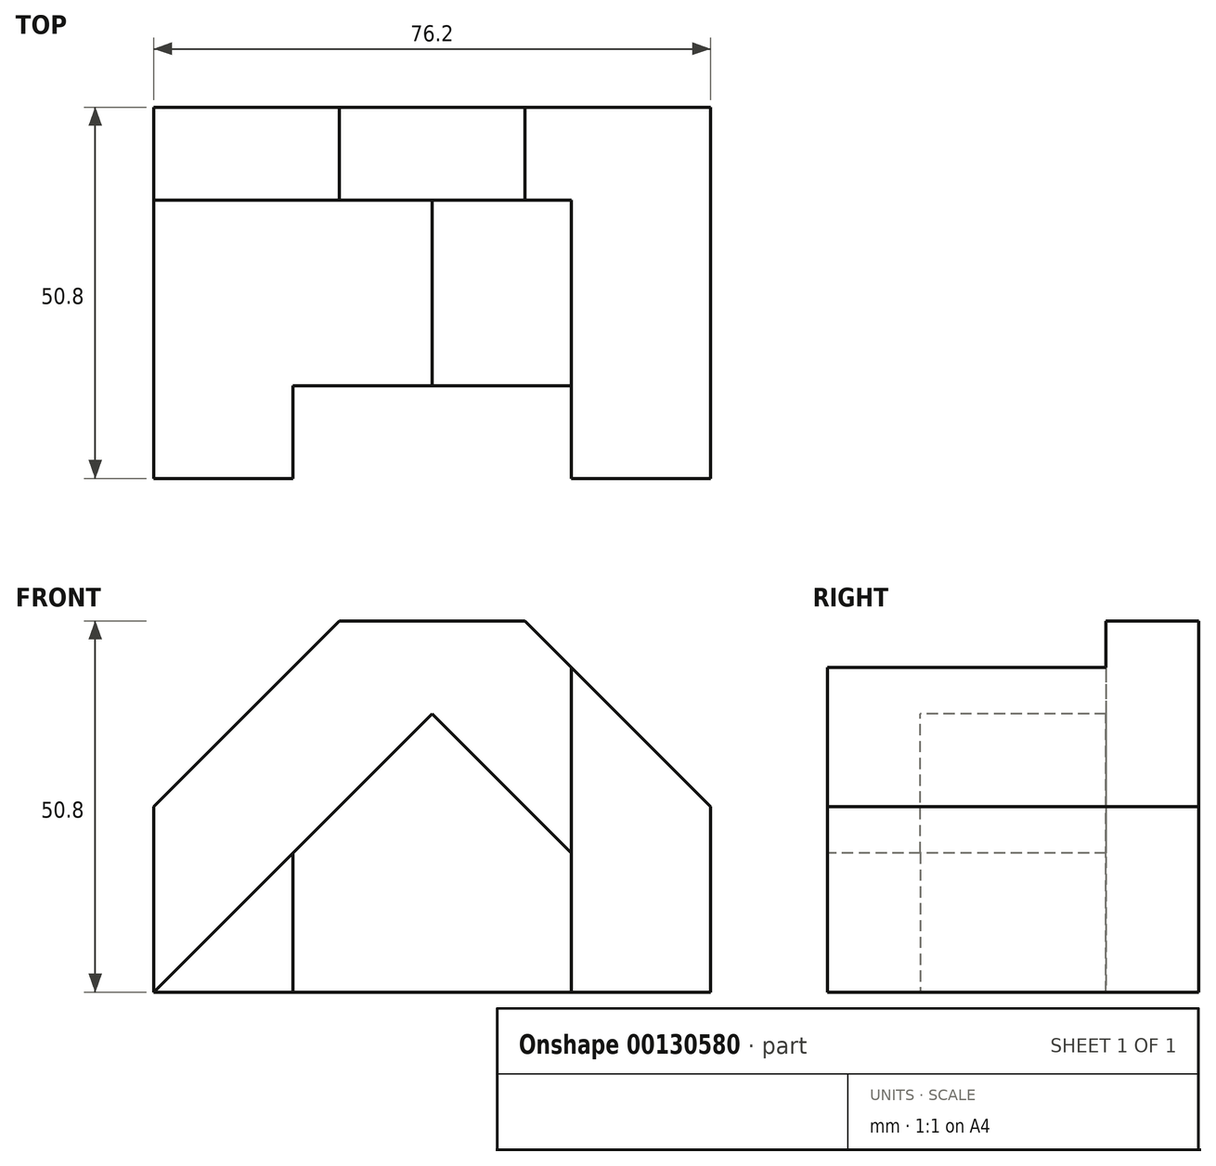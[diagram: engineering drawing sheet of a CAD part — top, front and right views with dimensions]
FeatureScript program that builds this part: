
annotation { "Feature Type Name" : "Feature", "Feature Type Description" : "" }
export const myFeature = defineFeature(function(context is Context, id is Id, definition is map)
    precondition{}
    {
        {
            var Q0;
            Q0=qCreatedBy(makeId("Top.planeOp"),FACE);
            var sketch = newSketch(context, id + "F0", { "sketchPlane" : qUnion([Q0])});
            skLineSegment(sketch, "E0", {"start": v(0, 0) * mm, "end": v(-38.1, 0) * mm});
            skLineSegment(sketch, "E1", {"start": v(-38.1, 0) * mm, "end": v(-38.1, 12.7) * mm});
            skLineSegment(sketch, "E2", {"start": v(-38.1, 12.7) * mm, "end": v(38.1, 12.7) * mm});
            skLineSegment(sketch, "E3", {"start": v(38.1, 12.7) * mm, "end": v(38.1, 0) * mm});
            skLineSegment(sketch, "E4", {"start": v(38.1, 0) * mm, "end": v(0, 0) * mm});
            skLineSegment(sketch, "E5", {"start": v(-19.05, 0) * mm, "end": v(-19.05, 12.7) * mm});
            skLineSegment(sketch, "E6", {"start": v(6.35, 12.7) * mm, "end": v(6.35, 0) * mm});
            skLineSegment(sketch, "E7", {"start": v(-38.1, 0) * mm, "end": v(-38.1, -38.1) * mm});
            skLineSegment(sketch, "E8", {"start": v(38.1, -38.1) * mm, "end": v(38.1, 0) * mm});
            skLineSegment(sketch, "E9", {"start": v(-38.1, -38.1) * mm, "end": v(-19.05, -38.1) * mm});
            skLineSegment(sketch, "E10", {"start": v(-19.05, -38.1) * mm, "end": v(-19.05, -25.4) * mm});
            skLineSegment(sketch, "E11", {"start": v(-19.05, -25.4) * mm, "end": v(19.05, -25.4) * mm});
            skLineSegment(sketch, "E12", {"start": v(19.05, -25.4) * mm, "end": v(19.05, -38.1) * mm});
            skLineSegment(sketch, "E13", {"start": v(19.05, -38.1) * mm, "end": v(38.1, -38.1) * mm});
            skLineSegment(sketch, "E14", {"start": v(-38.1, -38.1) * mm, "end": v(0, 0) * mm});
            skLineSegment(sketch, "E15", {"start": v(0, 0) * mm, "end": v(38.1, -38.1) * mm});
            skSolve(sketch);
        }
        {
            var Q0;
            {var subQ0=sQuery(id+"F0.wireOp",EDGE,"E1");Q0=makeQuery(id+"F0.imprint","IMPRINT",FACE,{"disambiguationData":[TD([[makeQuery(id+"F0.imprint","IMPRINT",EDGE,{"derivedFrom":subQ0}),-1.0]])]});}
            var Q1;
            {var subQ0=sQuery(id+"F0.wireOp",EDGE,"E3");Q1=makeQuery(id+"F0.imprint","IMPRINT",FACE,{"disambiguationData":[TD([[makeQuery(id+"F0.imprint","IMPRINT",EDGE,{"derivedFrom":subQ0}),-1.0]])]});}
            var Q2;
            {var subQ0=sQuery(id+"F0.wireOp",EDGE,"E5");Q2=makeQuery(id+"F0.imprint","IMPRINT",FACE,{"disambiguationData":[TD([[makeQuery(id+"F0.imprint","IMPRINT",EDGE,{"derivedFrom":subQ0}),-1.0]])]});}
            var Q3;
            {var subQ0=sQuery(id+"F0.wireOp",EDGE,"E4");Q3=makeQuery(id+"F0.imprint","IMPRINT",FACE,{"disambiguationData":[TD([[makeQuery(id+"F0.imprint","IMPRINT",EDGE,{"derivedFrom":subQ0}),1.0]])]});}
            var Q4;
            {var subQ3=sQuery(id+"F0.wireOp",EDGE,"E7");Q4=makeQuery(id+"F0.imprint","IMPRINT",FACE,{"disambiguationData":[TD([[makeQuery(id+"F0.imprint","IMPRINT",EDGE,{"derivedFrom":subQ3}),1.0]])]});}
            var Q5;
            Q5=makeQuery(id+"F0.imprint","IMPRINT",FACE,{"disambiguationData":[TD([[makeQuery(id+"F0.imprint","IMPRINT",EDGE,{"derivedFrom":sQuery(id+"F0.wireOp",EDGE,"E9")}),1.0]])]});
            extrude(context, id + "F1", {"entities" : qUnion([Q0, Q1, Q2, Q3, Q4, Q5]), "depth" : 50.8 * mm});
        }
        {
            var Q0;
            Q0=makeQuery(id+"F1.opExtrude","SWEPT_FACE",FACE,{"disambiguationData":[OSD([sQuery(id+"F0.wireOp",EDGE,"E2")])]});
            var sketch = newSketch(context, id + "F2", { "sketchPlane" : qUnion([Q0])});
            skLineSegment(sketch, "E16", {"start": v(-38.1, 25.4) * mm, "end": v(-12.7, 50.8) * mm});
            skLineSegment(sketch, "E17", {"start": v(-12.7, 50.8) * mm, "end": v(12.7, 50.8) * mm});
            skLineSegment(sketch, "E18", {"start": v(12.7, 50.8) * mm, "end": v(38.1, 25.4) * mm});
            skSolve(sketch);
        }
        {
            var Q0;
            Q0 = qSketchRegion(id + "F2", true);
            var Q1;
            {var subQ0=sQuery(id+"F2.wireOp",EDGE,"E16");Q1=makeQuery(id+"F2.imprint","IMPRINT",FACE,{"disambiguationData":[TD([[makeQuery(id+"F2.imprint","IMPRINT",EDGE,{"derivedFrom":subQ0}),1.0]])]});}
            var Q2;
            {var subQ0=sQuery(id+"F2.wireOp",EDGE,"E18");Q2=makeQuery(id+"F2.imprint","IMPRINT",FACE,{"disambiguationData":[TD([[makeQuery(id+"F2.imprint","IMPRINT",EDGE,{"derivedFrom":subQ0}),1.0]])]});}
            extrude(context, id + "F3", {"entities" : qUnion([Q0, Q1, Q2]), "operationType" : NewBodyOperationType.REMOVE, "endBound" : BoundingType.THROUGH_ALL, "oppositeDirection" : true, "depth" : 25.4 * mm});
        }
        {
            var Q0;
            Q0=makeQuery(id+"F1.opExtrude","SWEPT_FACE",FACE,{"disambiguationData":[OSD([sQuery(id+"F0.wireOp",EDGE,"E9")])]});
            var sketch = newSketch(context, id + "F4", { "sketchPlane" : qUnion([Q0])});
            skLineSegment(sketch, "E19", {"start": v(-38.1, 0) * mm, "end": v(0, 38.1) * mm});
            skLineSegment(sketch, "E20", {"start": v(0, 38.1) * mm, "end": v(38.1, 0) * mm});
            skSolve(sketch);
        }
        {
            var Q0;
            Q0=makeQuery(id+"F1.opExtrude","SWEPT_FACE",FACE,{"disambiguationData":[OSD([sQuery(id+"F0.wireOp",EDGE,"E11")])]});
            var sketch = newSketch(context, id + "F5", { "sketchPlane" : qUnion([Q0])});
            skLineSegment(sketch, "E21", {"start": v(-19.05, 19.05) * mm, "end": v(0, 38.1) * mm});
            skLineSegment(sketch, "E22", {"start": v(0, 38.1) * mm, "end": v(19.05, 19.05) * mm});
            skPoint(sketch, "E23", {"position": v(-19.05, 22.23) * mm});
            skSolve(sketch);
        }
        {
            var Q0;
            Q0=makeQuery(id+"F1.opExtrude","SWEPT_FACE",FACE,{"disambiguationData":[OSD([sQuery(id+"F0.wireOp",EDGE,"E13")])]});
            var sketch = newSketch(context, id + "F6", { "sketchPlane" : qUnion([Q0])});
            skLineSegment(sketch, "E24", {"start": v(38.1, 0) * mm, "end": v(19.05, 19.05) * mm});
            skSolve(sketch);
        }
        {
            var Q0;
            {var subQ1=sQuery(id+"F0.wireOp",EDGE,"E9");var subQ5=makeQuery(id+"F3.boolean.opBoolean","INTERSECT",EDGE,{"derivedFrom":[makeQuery(id+"F1.opExtrude","SWEPT_FACE",FACE,{"disambiguationData":[OSD([subQ1])]}),makeQuery(id+"F3.opExtrude","SWEPT_FACE",FACE,{"disambiguationData":[OSD([sQuery(id+"F2.wireOp",EDGE,"E18")])]})]});Q0=makeQuery(id+"F4.imprint","IMPRINT",FACE,{"disambiguationData":[TD([[makeQuery(id+"F4.imprint","IMPRINT",EDGE,{"derivedFrom":subQ5}),1.0]])]});}
            var Q1;
            {var subQ0=sQuery(id+"F6.wireOp",EDGE,"5XodOkcT-aZFN-8eT7-S5IH-uYk0JnqQcXSi");Q1=makeQuery(id+"F6.imprint","IMPRINT",FACE,{"disambiguationData":[TD([[makeQuery(id+"F6.imprint","IMPRINT",EDGE,{"derivedFrom":subQ0}),-1.0]])]});}
            extrude(context, id + "F7", {"entities" : qUnion([Q0, Q1]), "operationType" : NewBodyOperationType.REMOVE, "oppositeDirection" : true, "depth" : 38.1 * mm});
        }
        {
            var Q0;
            {var subQ4=sQuery(id+"F5.wireOp",EDGE,"E21");Q0=makeQuery(id+"F5.imprint","IMPRINT",FACE,{"disambiguationData":[TD([[makeQuery(id+"F5.imprint","IMPRINT",EDGE,{"derivedFrom":subQ4}),1.0]])]});}
            extrude(context, id + "F8", {"entities" : qUnion([Q0]), "operationType" : NewBodyOperationType.REMOVE, "oppositeDirection" : true, "depth" : 25.4 * mm});
        }
    });
